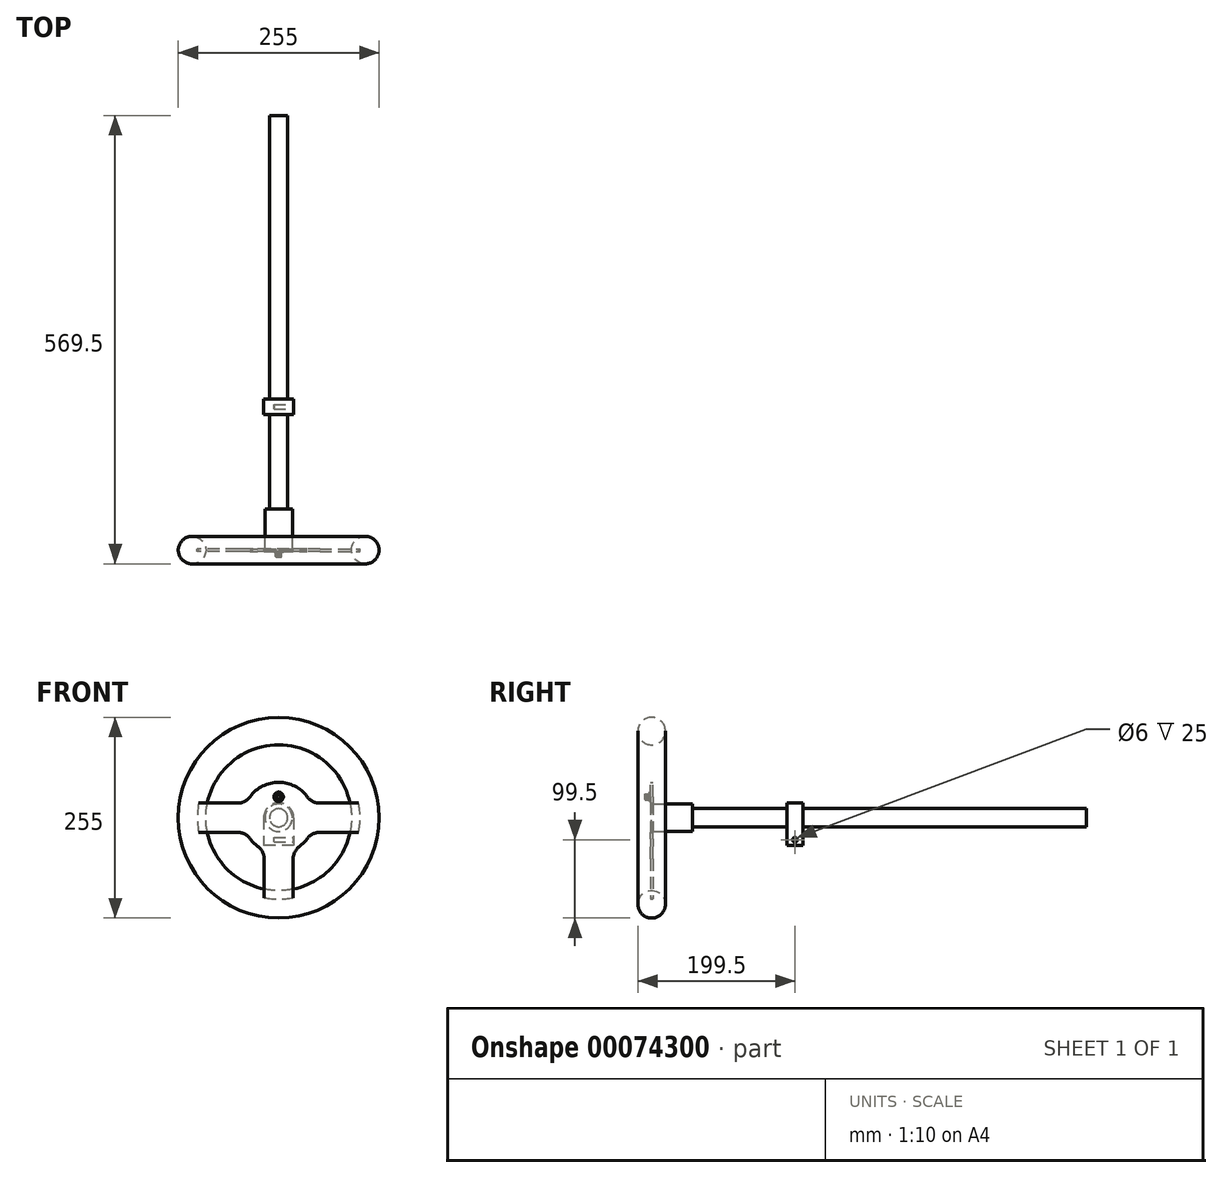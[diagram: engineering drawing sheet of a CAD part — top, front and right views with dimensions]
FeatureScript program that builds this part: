
annotation { "Feature Type Name" : "Feature", "Feature Type Description" : "" }
export const myFeature = defineFeature(function(context is Context, id is Id, definition is map)
    precondition{}
    {
        {
            var Q0;
            Q0=qCreatedBy(makeId("Front.planeOp"),FACE);
            var sketch = newSketch(context, id + "F0", { "sketchPlane" : qUnion([Q0])});
            skCircle(sketch, "E0", {"center": v(0, 0) * mm, "radius": 11.5 * mm});
            skSolve(sketch);
        }
        {
            var Q0;
            Q0 = qSketchRegion(id + "F0", true);
            extrude(context, id + "F1", {"entities" : qUnion([Q0]), "depth" : 500 * mm});
        }
        {
            var Q0;
            Q0=makeQuery(id+"F1.opExtrude","CAP_FACE",FACE,{"disambiguationData":[OSD([sQuery(id+"F0.wireOp",EDGE,"E0")])],"isStart":false});
            var sketch = newSketch(context, id + "F2", { "sketchPlane" : qUnion([Q0])});
            skCircle(sketch, "E1", {"center": v(0, 0) * mm, "radius": 17.5 * mm});
            skSolve(sketch);
        }
        {
            var Q0;
            Q0 = qSketchRegion(id + "F2", true);
            extrude(context, id + "F3", {"entities" : qUnion([Q0]), "operationType" : NewBodyOperationType.ADD, "depth" : 52 * mm});
        }
        {
            var Q0;
            Q0=makeQuery(id+"F3.opExtrude","CAP_FACE",FACE,{"disambiguationData":[OSD([sQuery(id+"F2.wireOp",EDGE,"E1")])],"isStart":false});
            var sketch = newSketch(context, id + "F4", { "sketchPlane" : qUnion([Q0])});
            skCircle(sketch, "E2.0", {"center": v(0, 0) * mm, "radius": 17.5 * mm});
            skSolve(sketch);
        }
        {
            var Q0;
            Q0=qCreatedBy(makeId("Right.planeOp"),FACE);
            var sketch = newSketch(context, id + "F5", { "sketchPlane" : qUnion([Q0])});
            skLineSegment(sketch, "E3.0", {"start": v(-552, -17.5) * mm, "end": v(-552, 17.5) * mm, "construction": true});
            skLineSegment(sketch, "E4", {"start": v(-552, 17.5) * mm, "end": v(-552, 169.8) * mm, "construction": true});
            skCircle(sketch, "E5", {"center": v(-552, 110) * mm, "radius": 17.5 * mm});
            skLineSegment(sketch, "E6", {"start": v(-552, 0) * mm, "end": v(-620.4, 0) * mm, "construction": true});
            skPoint(sketch, "E6.endSnap0", {"position": v(-552, 0) * mm});
            skSolve(sketch);
        }
        {
            var Q0;
            Q0=makeQuery(id+"F5.imprint","IMPRINT",FACE,{"disambiguationData":[TD([[makeQuery(id+"F5.imprint","IMPRINT",EDGE,{"derivedFrom":sQuery(id+"F5.wireOp",EDGE,"E5")}),1.0]])]});
            var Q1;
            Q1=sQuery(id+"F5.wireOp",EDGE,"E6");
            revolve(context, id + "F6", {"entities" : qUnion([Q0]), "axis" : qUnion([Q1]), "revolveType" : RevolveType.FULL});
        }
        {
            var Q0;
            Q0=makeQuery(id+"F4.imprint","IMPRINT",FACE,{"disambiguationData":[TD([[makeQuery(id+"F4.imprint","IMPRINT",EDGE,{"derivedFrom":sQuery(id+"F4.wireOp",EDGE,"E2.0")}),1.0]])]});
            var sketch = newSketch(context, id + "F7", { "sketchPlane" : qUnion([Q0])});
            skArc(sketch, "E7", {"start": v(-36.26, -26.65) * mm, "mid": v(-31.82, -31.82) * mm, "end": v(-26.65, -36.26) * mm});
            skLineSegment(sketch, "E8", {"start": v(0, 0) * mm, "end": v(-180.98, 0) * mm, "construction": true});
            skLineSegment(sketch, "E9", {"start": v(0, 0) * mm, "end": v(167.46, 0) * mm, "construction": true});
            skLineSegment(sketch, "E10", {"start": v(0, 0) * mm, "end": v(0, -141.77) * mm, "construction": true});
            skArc(sketch, "E11", {"start": v(-101.65, 18.5) * mm, "mid": v(-103.32, 0) * mm, "end": v(-101.65, -18.5) * mm});
            skLineSegment(sketch, "E12.0", {"start": v(-52.37, 18.5) * mm, "end": v(-101.65, 18.5) * mm});
            skLineSegment(sketch, "E12.1", {"start": v(52.37, 18.5) * mm, "end": v(101.65, 18.5) * mm});
            skLineSegment(sketch, "E13.0", {"start": v(-52.37, -18.5) * mm, "end": v(-101.65, -18.5) * mm});
            skLineSegment(sketch, "E14.0", {"start": v(18.5, -52.37) * mm, "end": v(18.5, -101.65) * mm});
            skLineSegment(sketch, "E15.0", {"start": v(-18.5, -52.37) * mm, "end": v(-18.5, -101.65) * mm});
            skArc(sketch, "E16.trimOffspring", {"start": v(36.26, 26.65) * mm, "mid": v(0, 45) * mm, "end": v(-36.26, 26.65) * mm});
            skLineSegment(sketch, "E17.trimOffspring", {"start": v(52.37, -18.5) * mm, "end": v(101.65, -18.5) * mm});
            skArc(sketch, "E18.trimOffspring", {"start": v(101.65, -18.5) * mm, "mid": v(103.32, 0) * mm, "end": v(101.65, 18.5) * mm});
            skArc(sketch, "E19.trimOffspring", {"start": v(-18.5, -101.65) * mm, "mid": v(0, -103.32) * mm, "end": v(18.5, -101.65) * mm});
            skPoint(sketch, "E20.visualSharp", {"position": v(-41.02, 18.5) * mm});
            skArc(sketch, "E20.filletArc", {"start": v(-52.37, 18.5) * mm, "mid": v(-43.34, 20.65) * mm, "end": v(-36.26, 26.65) * mm});
            skPoint(sketch, "E21.visualSharp", {"position": v(41.02, 18.5) * mm});
            skArc(sketch, "E21.filletArc", {"start": v(36.26, 26.65) * mm, "mid": v(43.34, 20.65) * mm, "end": v(52.37, 18.5) * mm});
            skPoint(sketch, "E22.visualSharp", {"position": v(41.02, -18.5) * mm});
            skArc(sketch, "E22.filletArc", {"start": v(52.37, -18.5) * mm, "mid": v(43.34, -20.65) * mm, "end": v(36.26, -26.65) * mm});
            skPoint(sketch, "E23.visualSharp", {"position": v(-41.02, -18.5) * mm});
            skArc(sketch, "E23.filletArc", {"start": v(-36.26, -26.65) * mm, "mid": v(-43.34, -20.65) * mm, "end": v(-52.37, -18.5) * mm});
            skArc(sketch, "E24.trimOffspring", {"start": v(26.65, -36.26) * mm, "mid": v(31.82, -31.82) * mm, "end": v(36.26, -26.65) * mm});
            skPoint(sketch, "E25.visualSharp", {"position": v(-18.5, -41.02) * mm});
            skArc(sketch, "E25.filletArc", {"start": v(-18.5, -52.37) * mm, "mid": v(-20.65, -43.34) * mm, "end": v(-26.65, -36.26) * mm});
            skPoint(sketch, "E26.visualSharp", {"position": v(18.5, -41.02) * mm});
            skArc(sketch, "E26.filletArc", {"start": v(26.65, -36.26) * mm, "mid": v(20.65, -43.34) * mm, "end": v(18.5, -52.37) * mm});
            skSolve(sketch);
        }
        {
            var Q0;
            Q0 = qSketchRegion(id + "F7", true);
            extrude(context, id + "F8", {"entities" : qUnion([Q0]), "depth" : 3 * mm, "symmetric" : true});
        }
        {
            var Q0;
            Q0=makeQuery(id+"F3.opExtrude","CAP_FACE",FACE,{"disambiguationData":[OSD([sQuery(id+"F2.wireOp",EDGE,"E1")])],"isStart":true});
            cPlane(context, id + "F9", {"entities" : qUnion([Q0]), "cplaneType" : CPlaneType.OFFSET, "offset" : 120 * mm, "width" : 150 * mm, "height" : 150 * mm});
        }
        {
            var Q0;
            Q0=qCreatedBy(id+"F9.planeOp",FACE);
            var sketch = newSketch(context, id + "F10", { "sketchPlane" : qUnion([Q0])});
            skCircle(sketch, "E27.0", {"center": v(0, 0) * mm, "radius": 11.5 * mm});
            skArc(sketch, "E28", {"start": v(19, 0) * mm, "mid": v(0, 19) * mm, "end": v(-19, 0) * mm});
            skLineSegment(sketch, "E29", {"start": v(-19, 0) * mm, "end": v(-19, -35) * mm});
            skLineSegment(sketch, "E30", {"start": v(19, 0) * mm, "end": v(19, -35) * mm});
            skLineSegment(sketch, "E31", {"start": v(-19, -35) * mm, "end": v(19, -35) * mm});
            skPoint(sketch, "E32.orphan", {"position": v(19, -39.9) * mm});
            skSolve(sketch);
        }
        {
            var Q0;
            Q0 = qSketchRegion(id + "F10", true);
            extrude(context, id + "F11", {"entities" : qUnion([Q0]), "operationType" : NewBodyOperationType.ADD, "depth" : 20 * mm});
        }
        {
            var Q0;
            Q0=makeQuery(id+"F11.opExtrude","SWEPT_FACE",FACE,{"disambiguationData":[OSD([sQuery(id+"F10.wireOp",EDGE,"E29")])]});
            var sketch = newSketch(context, id + "F12", { "sketchPlane" : qUnion([Q0])});
            skCircle(sketch, "E33", {"center": v(-370, -28) * mm, "radius": 3 * mm});
            skPoint(sketch, "E33.centerSnap0", {"position": v(-370, -35) * mm});
            skSolve(sketch);
        }
        {
            var Q0;
            Q0 = qSketchRegion(id + "F12", true);
            extrude(context, id + "F13", {"entities" : qUnion([Q0]), "operationType" : NewBodyOperationType.REMOVE, "oppositeDirection" : true, "depth" : 25 * mm});
        }
        {
            var Q0;
            Q0=makeQuery(id+"F8.opExtrude","CAP_FACE",FACE,{"disambiguationData":[OSD([sQuery(id+"F7.wireOp",EDGE,"E7"),sQuery(id+"F7.wireOp",EDGE,"E11"),sQuery(id+"F7.wireOp",EDGE,"E12.0"),sQuery(id+"F7.wireOp",EDGE,"E12.1"),sQuery(id+"F7.wireOp",EDGE,"E13.0"),sQuery(id+"F7.wireOp",EDGE,"E14.0"),sQuery(id+"F7.wireOp",EDGE,"E15.0"),sQuery(id+"F7.wireOp",EDGE,"E16.trimOffspring"),sQuery(id+"F7.wireOp",EDGE,"E17.trimOffspring"),sQuery(id+"F7.wireOp",EDGE,"E18.trimOffspring"),sQuery(id+"F7.wireOp",EDGE,"E19.trimOffspring"),sQuery(id+"F7.wireOp",EDGE,"E20.filletArc"),sQuery(id+"F7.wireOp",EDGE,"E21.filletArc"),sQuery(id+"F7.wireOp",EDGE,"E22.filletArc"),sQuery(id+"F7.wireOp",EDGE,"E23.filletArc"),sQuery(id+"F7.wireOp",EDGE,"E24.trimOffspring"),sQuery(id+"F7.wireOp",EDGE,"E25.filletArc"),sQuery(id+"F7.wireOp",EDGE,"E26.filletArc")])],"isStart":false});
            var sketch = newSketch(context, id + "F14", { "sketchPlane" : qUnion([Q0])});
            skCircle(sketch, "E34", {"center": v(0, 26.52) * mm, "radius": 6 * mm});
            skSolve(sketch);
        }
        {
            var Q0;
            Q0 = qSketchRegion(id + "F14", true);
            extrude(context, id + "F15", {"entities" : qUnion([Q0]), "operationType" : NewBodyOperationType.ADD, "depth" : 1 * mm});
        }
        {
            var Q0;
            Q0=makeQuery(id+"F15.opExtrude","CAP_FACE",FACE,{"disambiguationData":[OSD([sQuery(id+"F14.wireOp",EDGE,"E34")])],"isStart":false});
            var sketch = newSketch(context, id + "F16", { "sketchPlane" : qUnion([Q0])});
            skCircle(sketch, "E35", {"center": v(0, 26.52) * mm, "radius": 4 * mm});
            skSolve(sketch);
        }
        {
            var Q0;
            Q0 = qSketchRegion(id + "F16", true);
            extrude(context, id + "F17", {"entities" : qUnion([Q0]), "operationType" : NewBodyOperationType.ADD, "depth" : 6 * mm});
        }
        {
            var Q0;
            Q0=makeQuery(id+"F17.opExtrude","CAP_FACE",FACE,{"disambiguationData":[OSD([sQuery(id+"F16.wireOp",EDGE,"E35")])],"isStart":false});
            var sketch = newSketch(context, id + "F18", { "sketchPlane" : qUnion([Q0])});
            skCircle(sketch, "E36.cCircle", {"center": v(0, 26.52) * mm, "radius": 2.59 * mm, "construction": true});
            skLineSegment(sketch, "E36.0", {"start": v(1.3, 29.22) * mm, "end": v(2.98, 26.75) * mm});
            skLineSegment(sketch, "E36.1", {"start": v(2.98, 26.75) * mm, "end": v(1.69, 24.05) * mm});
            skLineSegment(sketch, "E36.2", {"start": v(1.69, 24.05) * mm, "end": v(-1.3, 23.83) * mm});
            skLineSegment(sketch, "E36.3", {"start": v(-1.3, 23.83) * mm, "end": v(-2.98, 26.3) * mm});
            skLineSegment(sketch, "E36.4", {"start": v(-2.98, 26.3) * mm, "end": v(-1.69, 28.99) * mm});
            skLineSegment(sketch, "E36.5", {"start": v(-1.69, 28.99) * mm, "end": v(1.3, 29.22) * mm});
            skPoint(sketch, "E36.0.midPoint", {"position": v(2.14, 27.98) * mm});
            skSolve(sketch);
        }
        {
            var Q0;
            Q0 = qSketchRegion(id + "F18", true);
            var Q1;
            Q1=makeQuery(id+"F18.imprint","IMPRINT",FACE,{"disambiguationData":[TD([[makeQuery(id+"F18.imprint","IMPRINT",EDGE,{"derivedFrom":sQuery(id+"F18.wireOp",EDGE,"E36.0")}),-1.0]])]});
            extrude(context, id + "F19", {"entities" : qUnion([Q0, Q1]), "operationType" : NewBodyOperationType.REMOVE, "oppositeDirection" : true, "depth" : 4 * mm});
        }
        {
            var Q0;
            Q0=makeQuery(id+"F17.opExtrude","CAP_EDGE",EDGE,{"disambiguationData":[OSD([sQuery(id+"F16.wireOp",EDGE,"E35")])],"isStart":false});
            chamfer(context, id + "F20", {"entities" : qUnion([Q0]), "width" : 0.5 * mm, "tangentPropagation" : true});
        }
    });
